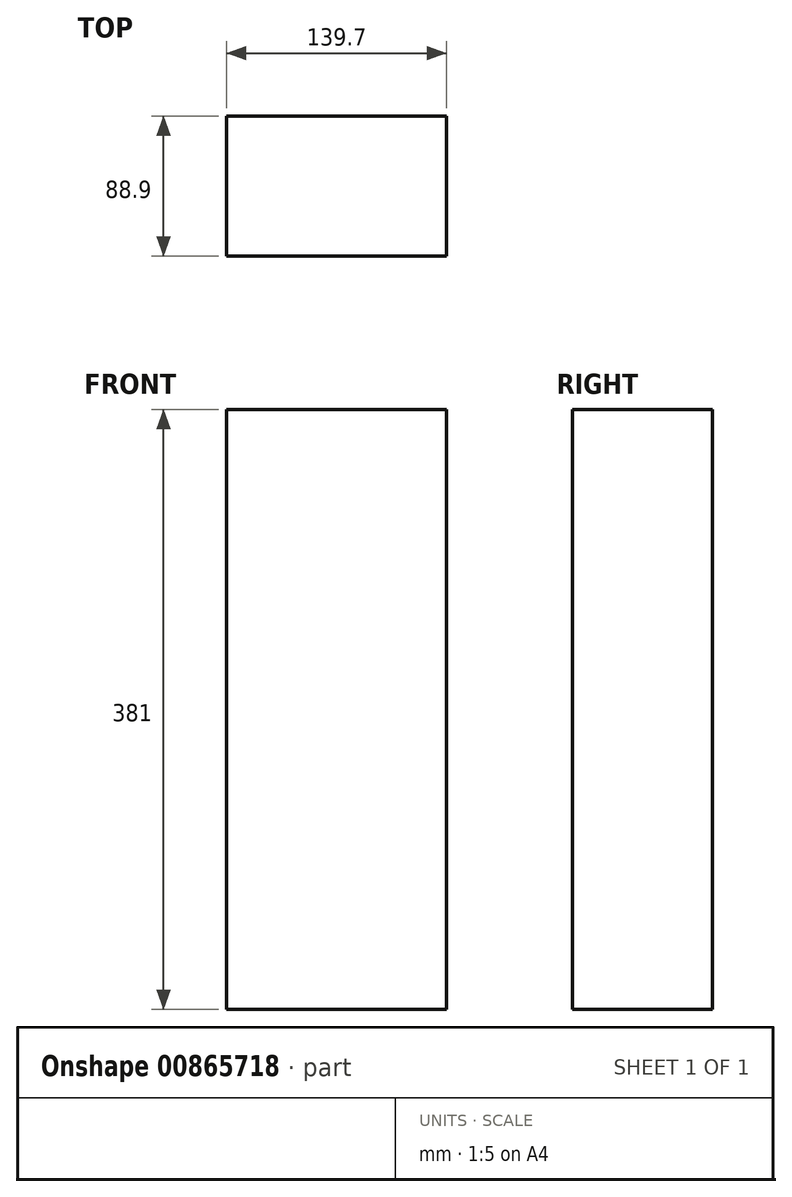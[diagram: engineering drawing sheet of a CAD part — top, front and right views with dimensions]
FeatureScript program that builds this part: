
annotation { "Feature Type Name" : "Feature", "Feature Type Description" : "" }
export const myFeature = defineFeature(function(context is Context, id is Id, definition is map)
    precondition{}
    {
        {
            var Q0;
            Q0=qCreatedBy(makeId("Top.planeOp"),FACE);
            var sketch = newSketch(context, id + "F0", { "sketchPlane" : qUnion([Q0])});
            skLineSegment(sketch, "E0.bottom", {"start": v(0, 0) * mm, "end": v(139.7, 0) * mm});
            skLineSegment(sketch, "E0.top", {"start": v(0, 88.9) * mm, "end": v(139.7, 88.9) * mm});
            skLineSegment(sketch, "E0.left", {"start": v(0, 0) * mm, "end": v(0, 88.9) * mm});
            skLineSegment(sketch, "E0.right", {"start": v(139.7, 0) * mm, "end": v(139.7, 88.9) * mm});
            skSolve(sketch);
        }
        {
            var Q0;
            Q0=makeQuery(id+"F0.imprint","IMPRINT",FACE,{"disambiguationData":[TD([[makeQuery(id+"F0.imprint","IMPRINT",EDGE,{"derivedFrom":sQuery(id+"F0.wireOp",EDGE,"E0.bottom")}),1.0]])]});
            extrude(context, id + "F1", {"entities" : qUnion([Q0]), "depth" : 381 * mm, "offsetDistance" : 25.4 * mm});
        }
    });
